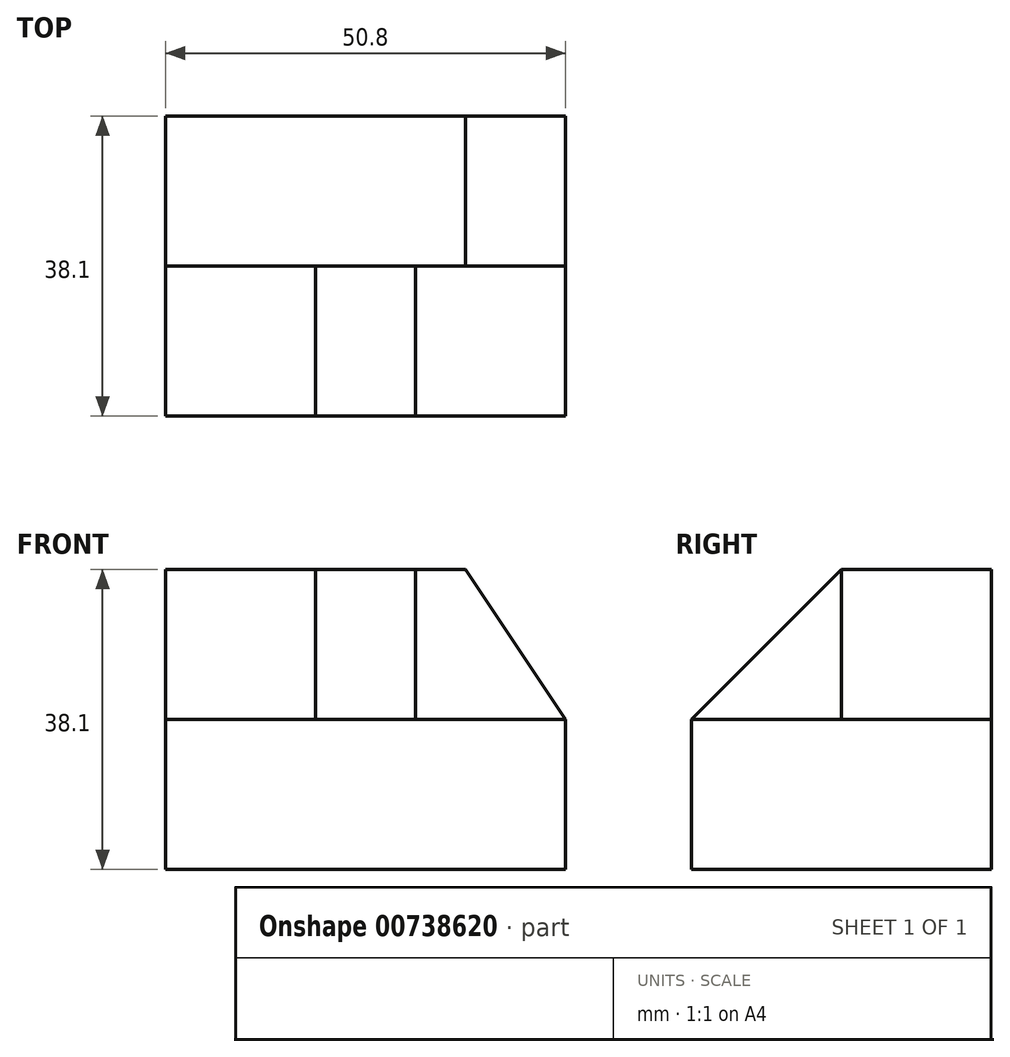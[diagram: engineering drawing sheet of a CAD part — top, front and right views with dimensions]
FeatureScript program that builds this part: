
annotation { "Feature Type Name" : "Feature", "Feature Type Description" : "" }
export const myFeature = defineFeature(function(context is Context, id is Id, definition is map)
    precondition{}
    {
        {
            var Q0;
            Q0=qCreatedBy(makeId("Top.planeOp"),FACE);
            var sketch = newSketch(context, id + "F0", { "sketchPlane" : qUnion([Q0])});
            skLineSegment(sketch, "E0.bottom", {"start": v(0, 0) * mm, "end": v(50.8, 0) * mm});
            skLineSegment(sketch, "E0.top", {"start": v(0, 38.1) * mm, "end": v(50.8, 38.1) * mm});
            skLineSegment(sketch, "E0.left", {"start": v(0, 0) * mm, "end": v(0, 38.1) * mm});
            skLineSegment(sketch, "E0.right", {"start": v(50.8, 0) * mm, "end": v(50.8, 38.1) * mm});
            skSolve(sketch);
        }
        {
            var Q0;
            Q0 = qSketchRegion(id + "F0", true);
            extrude(context, id + "F1", {"entities" : qUnion([Q0]), "depth" : 38.1 * mm, "offsetDistance" : 25.4 * mm});
        }
        {
            var Q0;
            Q0=makeQuery(id+"F1.opExtrude","SWEPT_FACE",FACE,{"disambiguationData":[OSD([sQuery(id+"F0.wireOp",EDGE,"E0.left")])]});
            var sketch = newSketch(context, id + "F2", { "sketchPlane" : qUnion([Q0])});
            skLineSegment(sketch, "E1.bottom", {"start": v(0, 38.1) * mm, "end": v(-19.05, 38.1) * mm});
            skLineSegment(sketch, "E1.top", {"start": v(0, 19.05) * mm, "end": v(-19.05, 19.05) * mm});
            skLineSegment(sketch, "E1.left", {"start": v(0, 38.1) * mm, "end": v(0, 19.05) * mm});
            skLineSegment(sketch, "E1.right", {"start": v(-19.05, 38.1) * mm, "end": v(-19.05, 19.05) * mm});
            skSolve(sketch);
        }
        {
            var Q0;
            Q0=makeQuery(id+"F2.imprint","IMPRINT",FACE,{"disambiguationData":[TD([[makeQuery(id+"F2.imprint","IMPRINT",EDGE,{"derivedFrom":sQuery(id+"F2.wireOp",EDGE,"E1.bottom")}),1.0]])]});
            extrude(context, id + "F3", {"entities" : qUnion([Q0]), "operationType" : NewBodyOperationType.REMOVE, "oppositeDirection" : true, "depth" : 19.05 * mm, "offsetDistance" : 25.4 * mm});
        }
        {
            var Q0;
            Q0=makeQuery(id+"F1.opExtrude","SWEPT_FACE",FACE,{"disambiguationData":[OSD([sQuery(id+"F0.wireOp",EDGE,"E0.right")])]});
            var sketch = newSketch(context, id + "F4", { "sketchPlane" : qUnion([Q0])});
            skLineSegment(sketch, "E2.bottom", {"start": v(0, 38.1) * mm, "end": v(19.05, 38.1) * mm});
            skLineSegment(sketch, "E2.top", {"start": v(0, 19.05) * mm, "end": v(19.05, 19.05) * mm});
            skLineSegment(sketch, "E2.left", {"start": v(0, 38.1) * mm, "end": v(0, 19.05) * mm});
            skLineSegment(sketch, "E2.right", {"start": v(19.05, 38.1) * mm, "end": v(19.05, 19.05) * mm});
            skSolve(sketch);
        }
        {
            var Q0;
            Q0=makeQuery(id+"F4.imprint","IMPRINT",FACE,{"disambiguationData":[TD([[makeQuery(id+"F4.imprint","IMPRINT",EDGE,{"derivedFrom":sQuery(id+"F4.wireOp",EDGE,"E2.bottom")}),-1.0]])]});
            extrude(context, id + "F5", {"entities" : qUnion([Q0]), "operationType" : NewBodyOperationType.REMOVE, "oppositeDirection" : true, "depth" : 19.05 * mm, "offsetDistance" : 25.4 * mm});
        }
        {
            var Q0;
            Q0=makeQuery(id+"F5.boolean.opBoolean","COPY",FACE,{"derivedFrom":makeQuery(id+"F5.opExtrude","CAP_FACE",FACE,{"disambiguationData":[OSD([sQuery(id+"F4.wireOp",EDGE,"E2.bottom"),sQuery(id+"F4.wireOp",EDGE,"E2.top"),sQuery(id+"F4.wireOp",EDGE,"E2.left"),sQuery(id+"F4.wireOp",EDGE,"E2.right")])],"isStart":false})});
            var sketch = newSketch(context, id + "F6", { "sketchPlane" : qUnion([Q0])});
            skLineSegment(sketch, "E3", {"start": v(0, 19.05) * mm, "end": v(19.05, 38.1) * mm});
            skSolve(sketch);
        }
        {
            var Q0;
            Q0=makeQuery(id+"F6.imprint","IMPRINT",FACE,{"disambiguationData":[TD([[makeQuery(id+"F6.imprint","IMPRINT",EDGE,{"derivedFrom":sQuery(id+"F6.wireOp",EDGE,"E3")}),1.0]])]});
            extrude(context, id + "F7", {"entities" : qUnion([Q0]), "operationType" : NewBodyOperationType.REMOVE, "endBound" : BoundingType.THROUGH_ALL, "oppositeDirection" : true, "depth" : 25.4 * mm, "offsetDistance" : 25.4 * mm});
        }
        {
            var Q0;
            Q0=makeQuery(id+"F5.boolean.opBoolean","COPY",FACE,{"derivedFrom":makeQuery(id+"F5.opExtrude","SWEPT_FACE",FACE,{"disambiguationData":[OSD([sQuery(id+"F4.wireOp",EDGE,"E2.right")])]})});
            var sketch = newSketch(context, id + "F8", { "sketchPlane" : qUnion([Q0])});
            skLineSegment(sketch, "E4", {"start": v(31.75, 38.1) * mm, "end": v(38.1, 38.1) * mm});
            skLineSegment(sketch, "E5", {"start": v(38.1, 38.1) * mm, "end": v(50.8, 19.05) * mm});
            skSolve(sketch);
        }
        {
            var Q0;
            {var subQ0=sQuery(id+"F8.wireOp",EDGE,"E5");Q0=makeQuery(id+"F8.imprint","IMPRINT",FACE,{"disambiguationData":[TD([[makeQuery(id+"F8.imprint","IMPRINT",EDGE,{"derivedFrom":subQ0}),1.0]])]});}
            extrude(context, id + "F9", {"entities" : qUnion([Q0]), "operationType" : NewBodyOperationType.REMOVE, "endBound" : BoundingType.THROUGH_ALL, "oppositeDirection" : true, "depth" : 25.4 * mm, "offsetDistance" : 25.4 * mm});
        }
    });
